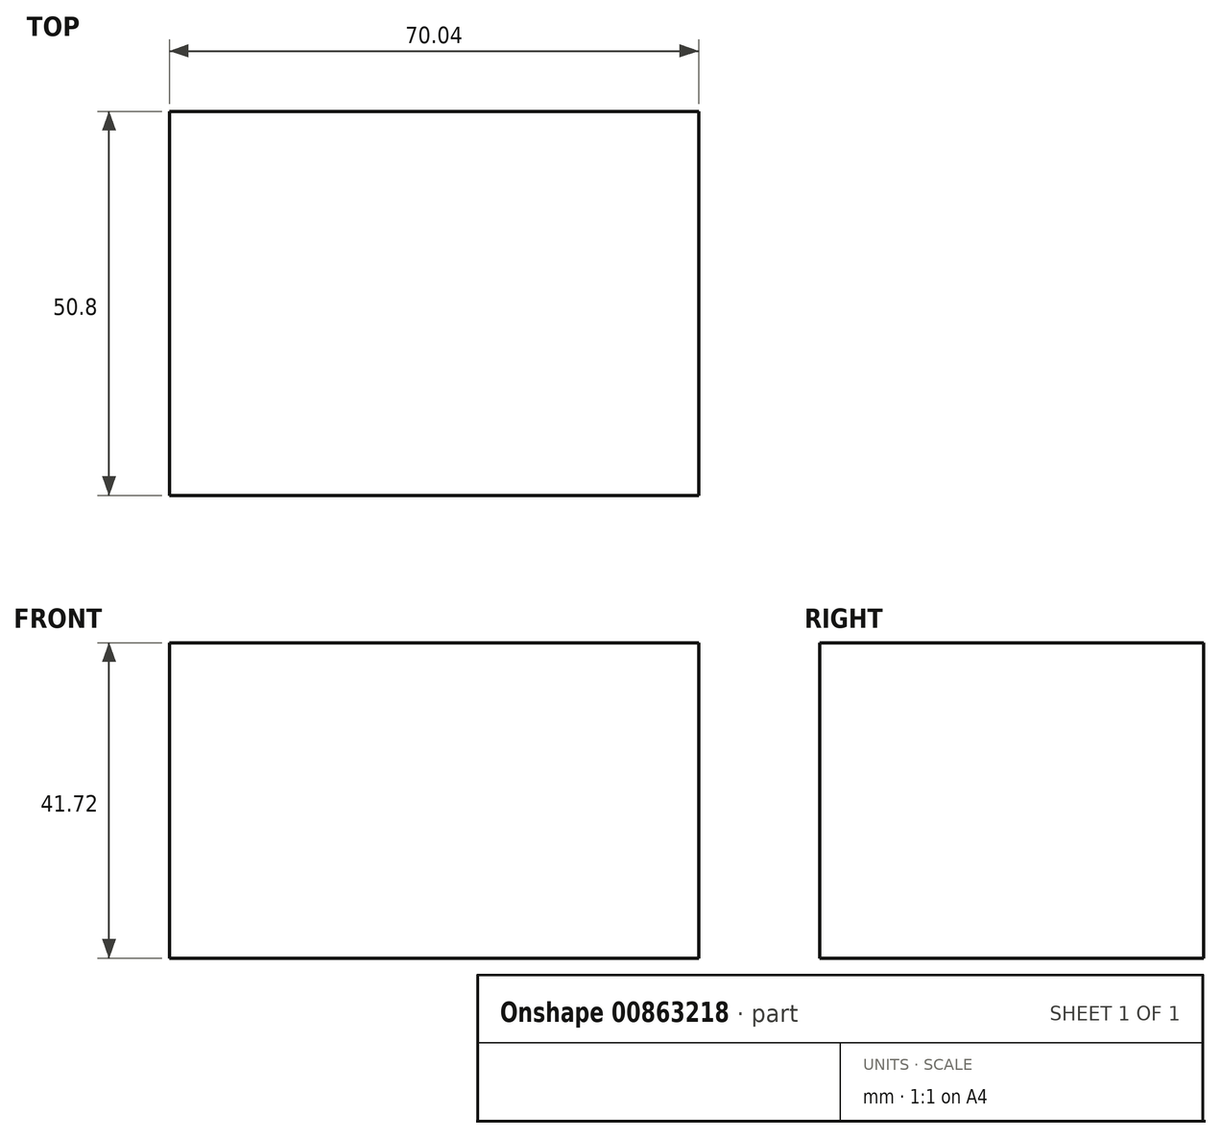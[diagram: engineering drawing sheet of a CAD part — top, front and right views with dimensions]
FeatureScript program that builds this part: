
annotation { "Feature Type Name" : "Feature", "Feature Type Description" : "" }
export const myFeature = defineFeature(function(context is Context, id is Id, definition is map)
    precondition{}
    {
        {
            var Q0;
            Q0=qCreatedBy(makeId("Front.planeOp"),FACE);
            var sketch = newSketch(context, id + "F0", { "sketchPlane" : qUnion([Q0])});
            skLineSegment(sketch, "E0.bottom", {"start": v(0, 0) * mm, "end": v(70.04, 0) * mm});
            skLineSegment(sketch, "E0.top", {"start": v(0, 41.72) * mm, "end": v(70.04, 41.72) * mm});
            skLineSegment(sketch, "E0.left", {"start": v(0, 0) * mm, "end": v(0, 41.72) * mm});
            skLineSegment(sketch, "E0.right", {"start": v(70.04, 0) * mm, "end": v(70.04, 41.72) * mm});
            skSolve(sketch);
        }
        {
            var Q0;
            Q0=makeQuery(id+"F0.imprint","IMPRINT",FACE,{"disambiguationData":[TD([[makeQuery(id+"F0.imprint","IMPRINT",EDGE,{"derivedFrom":sQuery(id+"F0.wireOp",EDGE,"E0.bottom")}),1.0]])]});
            extrude(context, id + "F1", {"entities" : qUnion([Q0]), "depth" : 50.8 * mm, "offsetDistance" : 25.4 * mm});
        }
    });
